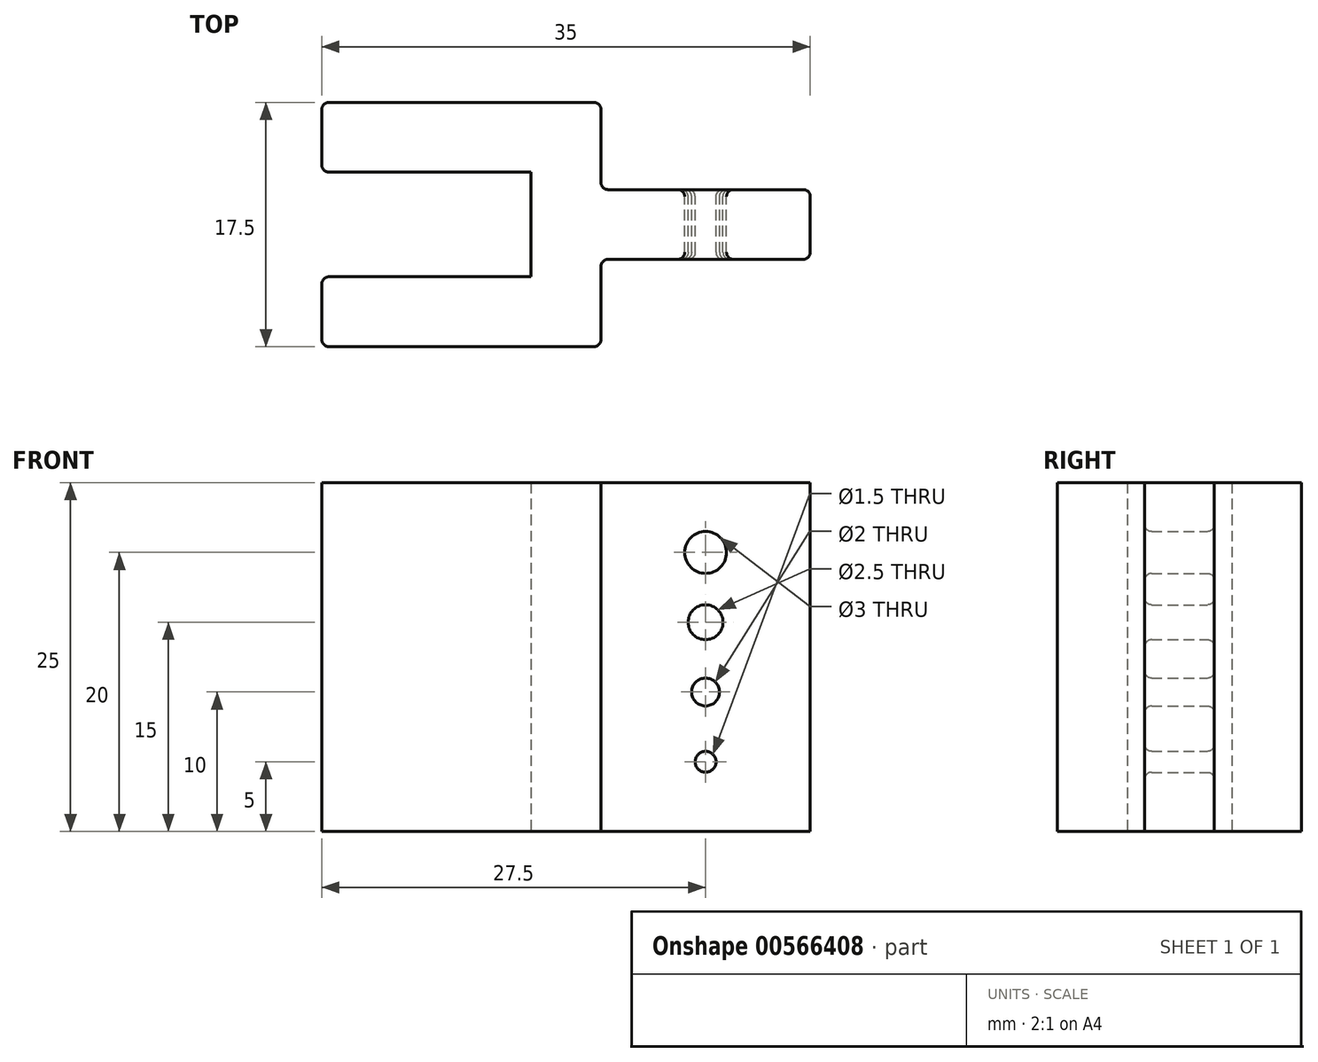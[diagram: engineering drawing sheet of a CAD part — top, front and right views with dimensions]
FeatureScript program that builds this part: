
annotation { "Feature Type Name" : "Feature", "Feature Type Description" : "" }
export const myFeature = defineFeature(function(context is Context, id is Id, definition is map)
    precondition{}
    {
        {
            var Q0;
            Q0=qCreatedBy(makeId("Top.planeOp"),FACE);
            var sketch = newSketch(context, id + "F0", { "sketchPlane" : qUnion([Q0])});
            skLineSegment(sketch, "E0.bottom", {"start": v(2.5, -8.75) * mm, "end": v(-2.5, -8.75) * mm});
            skLineSegment(sketch, "E0.top", {"start": v(2.5, 8.75) * mm, "end": v(-2.5, 8.75) * mm});
            skLineSegment(sketch, "E0.left", {"start": v(2.5, -8.75) * mm, "end": v(2.5, 8.75) * mm});
            skLineSegment(sketch, "E0.right", {"start": v(-2.5, -8.75) * mm, "end": v(-2.5, 8.75) * mm});
            skPoint(sketch, "E0.middle", {"position": v(0, 0) * mm});
            skLineSegment(sketch, "E1.bottom", {"start": v(-2.5, 8.75) * mm, "end": v(-17.5, 8.75) * mm});
            skLineSegment(sketch, "E1.top", {"start": v(-2.5, 3.75) * mm, "end": v(-17.5, 3.75) * mm});
            skLineSegment(sketch, "E1.left", {"start": v(-2.5, 8.75) * mm, "end": v(-2.5, 3.75) * mm});
            skLineSegment(sketch, "E1.right", {"start": v(-17.5, 8.75) * mm, "end": v(-17.5, 3.75) * mm});
            skLineSegment(sketch, "E2.bottom", {"start": v(-2.5, -8.75) * mm, "end": v(-17.5, -8.75) * mm});
            skLineSegment(sketch, "E2.top", {"start": v(-2.5, -3.75) * mm, "end": v(-17.5, -3.75) * mm});
            skLineSegment(sketch, "E2.left", {"start": v(-2.5, -8.75) * mm, "end": v(-2.5, -3.75) * mm});
            skLineSegment(sketch, "E2.right", {"start": v(-17.5, -8.75) * mm, "end": v(-17.5, -3.75) * mm});
            skLineSegment(sketch, "E3.bottom", {"start": v(2.5, -2.5) * mm, "end": v(17.5, -2.5) * mm});
            skLineSegment(sketch, "E3.top", {"start": v(2.5, 2.5) * mm, "end": v(17.5, 2.5) * mm});
            skLineSegment(sketch, "E3.left", {"start": v(2.5, -2.5) * mm, "end": v(2.5, 2.5) * mm});
            skLineSegment(sketch, "E3.right", {"start": v(17.5, -2.5) * mm, "end": v(17.5, 2.5) * mm});
            skSolve(sketch);
        }
        {
            var Q0;
            Q0 = qSketchRegion(id + "F0", true);
            extrude(context, id + "F1", {"entities" : qUnion([Q0]), "depth" : 25 * mm, "offsetDistance" : 25 * mm});
        }
        {
            var Q0;
            Q0=makeQuery(id+"F1.opExtrude","SWEPT_FACE",FACE,{"disambiguationData":[OSD([sQuery(id+"F0.wireOp",EDGE,"E3.top")])]});
            var sketch = newSketch(context, id + "F2", { "sketchPlane" : qUnion([Q0])});
            skLineSegment(sketch, "E4", {"start": v(-10, 25) * mm, "end": v(-10, 0) * mm, "construction": true});
            skCircle(sketch, "E5", {"center": v(-10, 20) * mm, "radius": 1.5 * mm});
            skCircle(sketch, "E6", {"center": v(-10, 15) * mm, "radius": 1.25 * mm});
            skCircle(sketch, "E7", {"center": v(-10, 10) * mm, "radius": 1 * mm});
            skCircle(sketch, "E8", {"center": v(-10, 5) * mm, "radius": 0.75 * mm});
            skSolve(sketch);
        }
        {
            var Q0;
            Q0 = qSketchRegion(id + "F2", true);
            extrude(context, id + "F3", {"entities" : qUnion([Q0]), "operationType" : NewBodyOperationType.REMOVE, "oppositeDirection" : true, "depth" : 25 * mm, "offsetDistance" : 25 * mm});
        }
        {
            var Q0;
            Q0=makeQuery(id+"F1.opExtrude","SWEPT_EDGE",EDGE,{"disambiguationData":[OSD([sQuery(id+"F0.wireOp",EDGE,"E0.top"),sQuery(id+"F0.wireOp",EDGE,"E0.left")])]});
            var Q1;
            Q1=makeQuery(id+"F1.opExtrude","SWEPT_EDGE",EDGE,{"disambiguationData":[OSD([sQuery(id+"F0.wireOp",EDGE,"E0.bottom"),sQuery(id+"F0.wireOp",EDGE,"E0.left")])]});
            var Q2;
            Q2=makeQuery(id+"F1.opExtrude","SWEPT_EDGE",EDGE,{"disambiguationData":[OSD([sQuery(id+"F0.wireOp",EDGE,"E3.top"),sQuery(id+"F0.wireOp",EDGE,"E3.right")])]});
            var Q3;
            Q3=makeQuery(id+"F1.opExtrude","SWEPT_EDGE",EDGE,{"disambiguationData":[OSD([sQuery(id+"F0.wireOp",EDGE,"E3.bottom"),sQuery(id+"F0.wireOp",EDGE,"E3.right")])]});
            var Q4;
            Q4=makeQuery(id+"F1.opExtrude","SWEPT_EDGE",EDGE,{"disambiguationData":[OSD([sQuery(id+"F0.wireOp",EDGE,"E1.bottom"),sQuery(id+"F0.wireOp",EDGE,"E1.right")])]});
            var Q5;
            Q5=makeQuery(id+"F1.opExtrude","SWEPT_EDGE",EDGE,{"disambiguationData":[OSD([sQuery(id+"F0.wireOp",EDGE,"E2.bottom"),sQuery(id+"F0.wireOp",EDGE,"E2.right")])]});
            var Q6;
            Q6=makeQuery(id+"F1.opExtrude","SWEPT_EDGE",EDGE,{"disambiguationData":[OSD([sQuery(id+"F0.wireOp",EDGE,"E2.top"),sQuery(id+"F0.wireOp",EDGE,"E2.right")])]});
            var Q7;
            Q7=makeQuery(id+"F1.opExtrude","SWEPT_EDGE",EDGE,{"disambiguationData":[OSD([sQuery(id+"F0.wireOp",EDGE,"E1.top"),sQuery(id+"F0.wireOp",EDGE,"E1.right")])]});
            var Q8;
            Q8=makeQuery(id+"F3.boolean.opBoolean","COPY",FACE,{"derivedFrom":makeQuery(id+"F3.opExtrude","SWEPT_FACE",FACE,{"disambiguationData":[OSD([sQuery(id+"F2.wireOp",EDGE,"E6")])]})});
            var Q9;
            Q9=makeQuery(id+"F3.boolean.opBoolean","COPY",FACE,{"derivedFrom":makeQuery(id+"F3.opExtrude","SWEPT_FACE",FACE,{"disambiguationData":[OSD([sQuery(id+"F2.wireOp",EDGE,"E7")])]})});
            var Q10;
            Q10=makeQuery(id+"F3.boolean.opBoolean","COPY",FACE,{"derivedFrom":makeQuery(id+"F3.opExtrude","SWEPT_FACE",FACE,{"disambiguationData":[OSD([sQuery(id+"F2.wireOp",EDGE,"E8")])]})});
            var Q11;
            Q11=makeQuery(id+"F3.boolean.opBoolean","COPY",FACE,{"derivedFrom":makeQuery(id+"F3.opExtrude","SWEPT_FACE",FACE,{"disambiguationData":[OSD([sQuery(id+"F2.wireOp",EDGE,"E5")])]})});
            var Q12;
            Q12=makeQuery(id+"F1.opExtrude","SWEPT_EDGE",EDGE,{"disambiguationData":[OSD([sQuery(id+"F0.wireOp",EDGE,"E0.left"),sQuery(id+"F0.wireOp",EDGE,"E3.top"),sQuery(id+"F0.wireOp",EDGE,"E3.left")])]});
            var Q13;
            Q13=makeQuery(id+"F1.opExtrude","SWEPT_EDGE",EDGE,{"disambiguationData":[OSD([sQuery(id+"F0.wireOp",EDGE,"E0.left"),sQuery(id+"F0.wireOp",EDGE,"E3.bottom"),sQuery(id+"F0.wireOp",EDGE,"E3.left")])]});
            fillet(context, id + "F4", {"entities" : qUnion([Q0, Q1, Q2, Q3, Q4, Q5, Q6, Q7, Q8, Q9, Q10, Q11, Q12, Q13]), "radius" : 0.5 * mm, "tangentPropagation" : true, "allowEdgeOverflow" : false});
        }
    });
